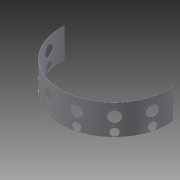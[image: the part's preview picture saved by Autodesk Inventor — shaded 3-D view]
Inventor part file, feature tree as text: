
AUTODESK INVENTOR PART (.ipt)
format: ipt  version: 2014 (Build 180170000, 170)  size: 787,968 bytes
history: native  units: in
note: dims shown in document units (in); Inventor stores cm internally (conversion verified against a paired STEP export)
features: sketch x7, hole x4, extrude x3, other x3, sheet_metal_op x2, thicken_offset x1
ambient origin geometry x8: Origin, YZ Plane, XZ Plane, XY Plane, X Axis, Y Axis, Z Axis, Center Point
bodies: Solid1 (feature_tree)
feature tree (20):
  thicken_offset  "Thicken1"
  sheet_metal_op  "Unfold4"
  hole  "spars"  [1 undecoded]
  hole  "supports"  [1 undecoded]
  hole  "rivets1"  [1 undecoded]
  hole  "Hole9"  [1 undecoded]
  extrude  "Extrusion4"  Depth=0.8108in
  sheet_metal_op  "Refold6"
  extrude  "Extrusion5"  Depth=1.3976in
  sketch  "Sketch1"  dims[d0=-1.5665in d1=73.1722in d2=10.0in d3=0.0in]
  other  "2D Equation Curve1"
  other  "Srf1"
  sketch  "Sketch2"  dims[d4=0.06in d5=0.06in]
  sketch  "Sketch3"  dims[d6=3.5433in d7=5.9in]
  sketch  "Sketch19"  dims[d8=5.9624in d9=2.3622in d11=9.4248in d12=0.3937in d14=1.0in]
  sketch  "Sketch20"  dims[d16=3.5433in d17=0.75in d18=0.375in d19=0.25in d20=0.5635in d21=0.06in d22=0.8108in]
  sketch  "Sketch22"  dims[d23=2.4803in d24=1.3976in]
  sketch  "Sketch23"  dims[d25=2.3622in d27=9.4248in d28=0.3937in d30=1.0in d32=5.9624in d33=2.4803in d34=0.75in d35=0.375in d36=0.25in d37=0.5635in d38=0.06in d39=0.8108in d212=0.5in d213=1.0in d214=1.1811in d216=4.0in d217=0.3937in d219=1.0in d221=0.0394in d222=0.75in d223=0.375in d224=0.25in d225=0.5635in d226=0.06in d227=0.8108in d228=1.25in d230=1.0in d231=0.5in d232=1.1811in d234=4.0in d235=0.3937in d237=1.0in d239=1.5in d240=0.0394in d241=0.75in d242=0.375in d243=0.25in d244=0.5635in d245=0.06in d246=0.8108in d247=0.02in d248=5.9624in d249=0.1in d250=0.0in d251=0.1304in d252=0.02in d253=0.1in d254=0.0in d255=4.1in d256=8.6024in d258=2.4815in]
  extrude  "ExtrusionSrf1"  Depth=5.9624in
  other  "Definition1"
note: 4 required parameter values undecoded (feature->parameter linkage not recoverable at this tier; creation-order binding heuristic only, values carry confidence <= 0.55)
